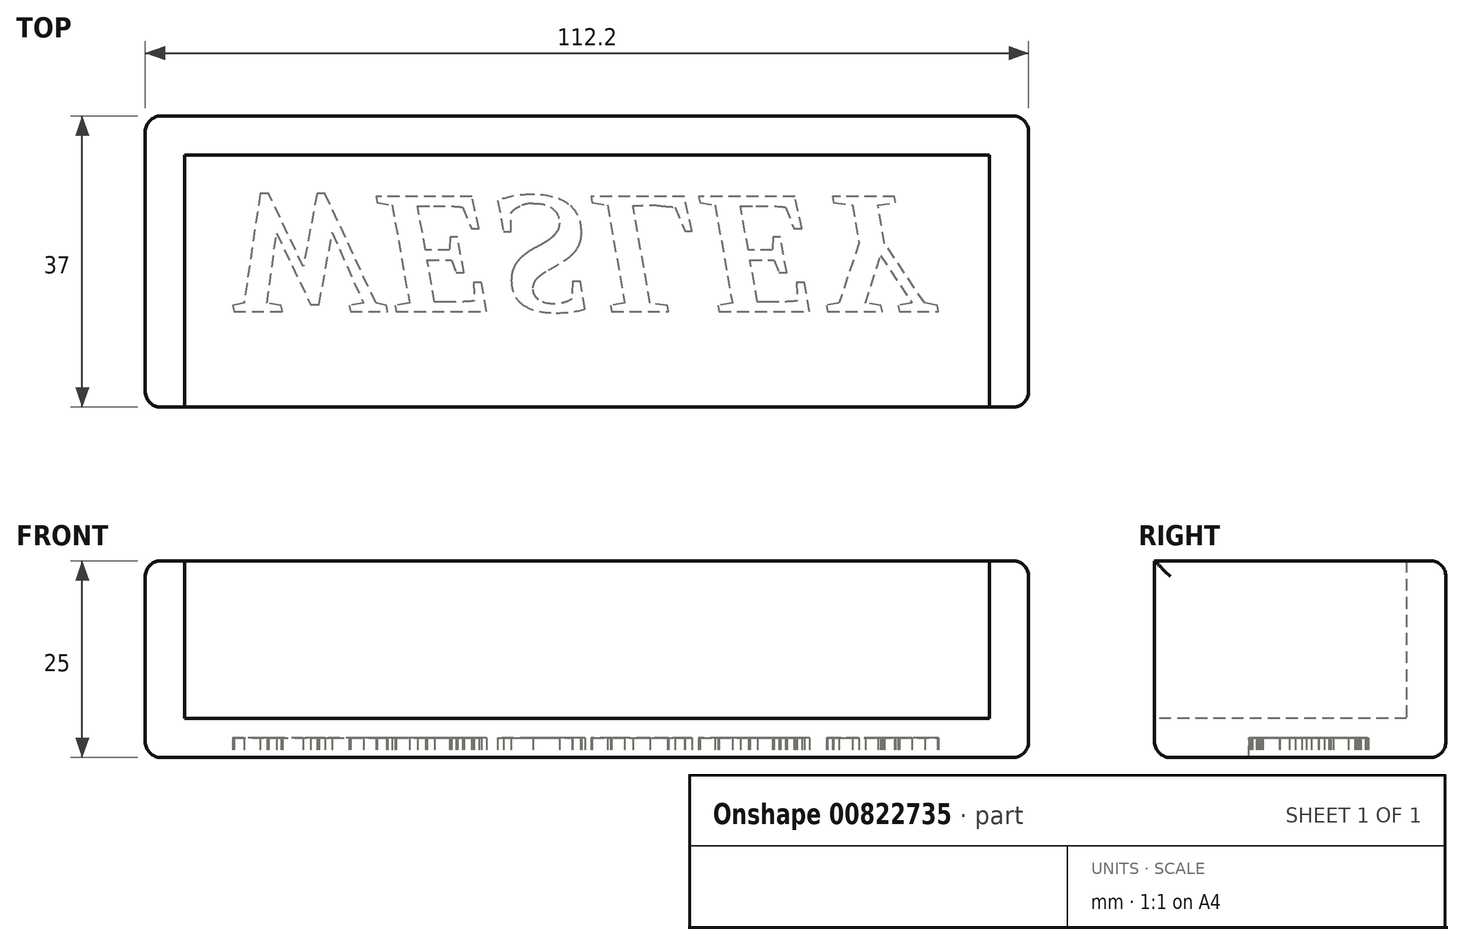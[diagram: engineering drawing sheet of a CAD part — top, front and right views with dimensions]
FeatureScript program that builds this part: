
annotation { "Feature Type Name" : "Feature", "Feature Type Description" : "" }
export const myFeature = defineFeature(function(context is Context, id is Id, definition is map)
    precondition{}
    {
        {
            var Q0;
            Q0=qCreatedBy(makeId("Top.planeOp"),FACE);
            var sketch = newSketch(context, id + "F0", { "sketchPlane" : qUnion([Q0])});
            skLineSegment(sketch, "E0.bottom", {"start": v(-26.8, 28.97) * mm, "end": v(75.4, 28.97) * mm});
            skLineSegment(sketch, "E0.top", {"start": v(-26.8, -3.03) * mm, "end": v(75.4, -3.03) * mm});
            skLineSegment(sketch, "E0.left", {"start": v(-26.8, 28.97) * mm, "end": v(-26.8, -3.03) * mm});
            skLineSegment(sketch, "E0.right", {"start": v(75.4, 28.97) * mm, "end": v(75.4, -3.03) * mm});
            skSolve(sketch);
        }
        {
            var Q0;
            Q0 = qSketchRegion(id + "F0", true);
            extrude(context, id + "F1", {"entities" : qUnion([Q0]), "depth" : 5 * mm, "offsetDistance" : 25 * mm});
        }
        {
            var Q0;
            Q0=makeQuery(id+"F1.opExtrude","SWEPT_FACE",FACE,{"disambiguationData":[OSD([sQuery(id+"F0.wireOp",EDGE,"E0.right")])]});
            var sketch = newSketch(context, id + "F2", { "sketchPlane" : qUnion([Q0])});
            skLineSegment(sketch, "E1.bottom", {"start": v(-3.03, 0) * mm, "end": v(28.97, 0) * mm});
            skLineSegment(sketch, "E1.top", {"start": v(-3.03, 25) * mm, "end": v(28.97, 25) * mm});
            skLineSegment(sketch, "E1.left", {"start": v(-3.03, 0) * mm, "end": v(-3.03, 25) * mm});
            skLineSegment(sketch, "E1.right", {"start": v(28.97, 0) * mm, "end": v(28.97, 25) * mm});
            skSolve(sketch);
        }
        {
            var Q0;
            Q0 = qSketchRegion(id + "F2", true);
            extrude(context, id + "F3", {"entities" : qUnion([Q0]), "operationType" : NewBodyOperationType.ADD, "depth" : 5 * mm, "offsetDistance" : 25 * mm});
        }
        {
            var Q0;
            Q0=makeQuery(id+"F1.opExtrude","SWEPT_FACE",FACE,{"disambiguationData":[OSD([sQuery(id+"F0.wireOp",EDGE,"E0.left")])]});
            var sketch = newSketch(context, id + "F4", { "sketchPlane" : qUnion([Q0])});
            skLineSegment(sketch, "E2.bottom", {"start": v(-28.97, 0) * mm, "end": v(3.03, 0) * mm});
            skLineSegment(sketch, "E2.top", {"start": v(-28.97, 25) * mm, "end": v(3.03, 25) * mm});
            skLineSegment(sketch, "E2.left", {"start": v(-28.97, 0) * mm, "end": v(-28.97, 25) * mm});
            skLineSegment(sketch, "E2.right", {"start": v(3.03, 0) * mm, "end": v(3.03, 25) * mm});
            skSolve(sketch);
        }
        {
            var Q0;
            Q0 = qSketchRegion(id + "F4", true);
            extrude(context, id + "F5", {"entities" : qUnion([Q0]), "operationType" : NewBodyOperationType.ADD, "depth" : 5 * mm, "offsetDistance" : 25 * mm});
        }
        {
            var Q0;
            Q0=makeQuery(id+"F5.boolean.opBoolean","MERGE",FACE,{"derivedFrom":[makeQuery(id+"F3.boolean.opBoolean","MERGE",FACE,{"derivedFrom":[makeQuery(id+"F1.opExtrude","SWEPT_FACE",FACE,{"disambiguationData":[OSD([sQuery(id+"F0.wireOp",EDGE,"E0.bottom")])]}),makeQuery(id+"F3.opExtrude","SWEPT_FACE",FACE,{"disambiguationData":[OSD([sQuery(id+"F2.wireOp",EDGE,"E1.right")])]})]}),makeQuery(id+"F5.opExtrude","SWEPT_FACE",FACE,{"disambiguationData":[OSD([sQuery(id+"F4.wireOp",EDGE,"E2.left")])]})]});
            var sketch = newSketch(context, id + "F6", { "sketchPlane" : qUnion([Q0])});
            skLineSegment(sketch, "E3.bottom", {"start": v(-80.4, 0) * mm, "end": v(31.8, 0) * mm});
            skLineSegment(sketch, "E3.top", {"start": v(-80.4, 25) * mm, "end": v(31.8, 25) * mm});
            skLineSegment(sketch, "E3.left", {"start": v(-80.4, 0) * mm, "end": v(-80.4, 25) * mm});
            skLineSegment(sketch, "E3.right", {"start": v(31.8, 0) * mm, "end": v(31.8, 25) * mm});
            skSolve(sketch);
        }
        {
            var Q0;
            Q0 = qSketchRegion(id + "F6", true);
            extrude(context, id + "F7", {"entities" : qUnion([Q0]), "operationType" : NewBodyOperationType.ADD, "depth" : 5 * mm, "offsetDistance" : 25 * mm});
        }
        {
            var Q0;
            Q0=makeQuery(id+"F7.boolean.opBoolean","MERGE",EDGE,{"derivedFrom":[makeQuery(id+"F5.opExtrude","CAP_EDGE",EDGE,{"disambiguationData":[OSD([sQuery(id+"F4.wireOp",EDGE,"E2.top")])],"isStart":false}),makeQuery(id+"F7.opExtrude","SWEPT_EDGE",EDGE,{"disambiguationData":[OSD([sQuery(id+"F6.wireOp",EDGE,"E3.top"),sQuery(id+"F6.wireOp",EDGE,"E3.right")])]})]});
            var Q1;
            Q1=makeQuery(id+"F7.boolean.opBoolean","MERGE",EDGE,{"derivedFrom":[makeQuery(id+"F3.opExtrude","CAP_EDGE",EDGE,{"disambiguationData":[OSD([sQuery(id+"F2.wireOp",EDGE,"E1.top")])],"isStart":false}),makeQuery(id+"F7.opExtrude","SWEPT_EDGE",EDGE,{"disambiguationData":[OSD([sQuery(id+"F6.wireOp",EDGE,"E3.top"),sQuery(id+"F6.wireOp",EDGE,"E3.left")])]})]});
            var Q2;
            Q2=makeQuery(id+"F7.opExtrude","CAP_EDGE",EDGE,{"disambiguationData":[OSD([sQuery(id+"F6.wireOp",EDGE,"E3.top")])],"isStart":false});
            var Q3;
            Q3=makeQuery(id+"F5.boolean.opBoolean","MERGE",EDGE,{"derivedFrom":[makeQuery(id+"F3.boolean.opBoolean","MERGE",EDGE,{"derivedFrom":[makeQuery(id+"F1.opExtrude","CAP_EDGE",EDGE,{"disambiguationData":[OSD([sQuery(id+"F0.wireOp",EDGE,"E0.top")])],"isStart":true}),makeQuery(id+"F3.opExtrude","SWEPT_EDGE",EDGE,{"disambiguationData":[OSD([sQuery(id+"F2.wireOp",EDGE,"E1.bottom"),sQuery(id+"F2.wireOp",EDGE,"E1.left")])]})]}),makeQuery(id+"F5.opExtrude","SWEPT_EDGE",EDGE,{"disambiguationData":[OSD([sQuery(id+"F4.wireOp",EDGE,"E2.bottom"),sQuery(id+"F4.wireOp",EDGE,"E2.right")])]})]});
            var Q4;
            Q4=makeQuery(id+"F7.boolean.opBoolean","MERGE",EDGE,{"derivedFrom":[makeQuery(id+"F5.opExtrude","CAP_EDGE",EDGE,{"disambiguationData":[OSD([sQuery(id+"F4.wireOp",EDGE,"E2.bottom")])],"isStart":false}),makeQuery(id+"F7.opExtrude","SWEPT_EDGE",EDGE,{"disambiguationData":[OSD([sQuery(id+"F6.wireOp",EDGE,"E3.bottom"),sQuery(id+"F6.wireOp",EDGE,"E3.right")])]})]});
            var Q5;
            Q5=makeQuery(id+"F5.opExtrude","CAP_EDGE",EDGE,{"disambiguationData":[OSD([sQuery(id+"F4.wireOp",EDGE,"E2.right")])],"isStart":false});
            var Q6;
            Q6=makeQuery(id+"F7.boolean.opBoolean","MERGE",EDGE,{"derivedFrom":[makeQuery(id+"F3.opExtrude","CAP_EDGE",EDGE,{"disambiguationData":[OSD([sQuery(id+"F2.wireOp",EDGE,"E1.bottom")])],"isStart":false}),makeQuery(id+"F7.opExtrude","SWEPT_EDGE",EDGE,{"disambiguationData":[OSD([sQuery(id+"F6.wireOp",EDGE,"E3.bottom"),sQuery(id+"F6.wireOp",EDGE,"E3.left")])]})]});
            var Q7;
            Q7=makeQuery(id+"F7.opExtrude","CAP_EDGE",EDGE,{"disambiguationData":[OSD([sQuery(id+"F6.wireOp",EDGE,"E3.bottom")])],"isStart":false});
            var Q8;
            Q8=makeQuery(id+"F7.opExtrude","CAP_EDGE",EDGE,{"disambiguationData":[OSD([sQuery(id+"F6.wireOp",EDGE,"E3.left")])],"isStart":false});
            var Q9;
            Q9=makeQuery(id+"F7.opExtrude","CAP_EDGE",EDGE,{"disambiguationData":[OSD([sQuery(id+"F6.wireOp",EDGE,"E3.right")])],"isStart":false});
            var Q10;
            Q10=makeQuery(id+"F3.opExtrude","CAP_EDGE",EDGE,{"disambiguationData":[OSD([sQuery(id+"F2.wireOp",EDGE,"E1.left")])],"isStart":false});
            fillet(context, id + "F8", {"entities" : qUnion([Q0, Q1, Q2, Q3, Q4, Q5, Q6, Q7, Q8, Q9, Q10]), "radius" : 2 * mm, "tangentPropagation" : true, "allowEdgeOverflow" : false});
        }
        {
            var Q0;
            Q0=makeQuery(id+"F7.boolean.opBoolean","MERGE",FACE,{"derivedFrom":[makeQuery(id+"F5.boolean.opBoolean","MERGE",FACE,{"derivedFrom":[makeQuery(id+"F3.boolean.opBoolean","MERGE",FACE,{"derivedFrom":[makeQuery(id+"F1.opExtrude","CAP_FACE",FACE,{"disambiguationData":[OSD([sQuery(id+"F0.wireOp",EDGE,"E0.bottom"),sQuery(id+"F0.wireOp",EDGE,"E0.top"),sQuery(id+"F0.wireOp",EDGE,"E0.left"),sQuery(id+"F0.wireOp",EDGE,"E0.right")])],"isStart":true}),makeQuery(id+"F3.opExtrude","SWEPT_FACE",FACE,{"disambiguationData":[OSD([sQuery(id+"F2.wireOp",EDGE,"E1.bottom")])]})]}),makeQuery(id+"F5.opExtrude","SWEPT_FACE",FACE,{"disambiguationData":[OSD([sQuery(id+"F4.wireOp",EDGE,"E2.bottom")])]})]}),makeQuery(id+"F7.opExtrude","SWEPT_FACE",FACE,{"disambiguationData":[OSD([sQuery(id+"F6.wireOp",EDGE,"E3.bottom")])]})]});
            var sketch = newSketch(context, id + "F9", { "sketchPlane" : qUnion([Q0])});
            skText(sketch, "E4", { "text": "WESLEY", "fontName": "Tinos-BoldItalic.ttf"});
            const initialGuessF9  = {"E4": [-0.02223, -0.02376, 1, 0, 0.0161]};
            skSetInitialGuess(sketch, initialGuessF9);
            skSolve(sketch);
        }
        {
            var Q0;
            Q0 = qSketchRegion(id + "F9", true);
            extrude(context, id + "F10", {"entities" : qUnion([Q0]), "operationType" : NewBodyOperationType.REMOVE, "oppositeDirection" : true, "depth" : 2.5 * mm, "offsetDistance" : 25 * mm});
        }
    });
